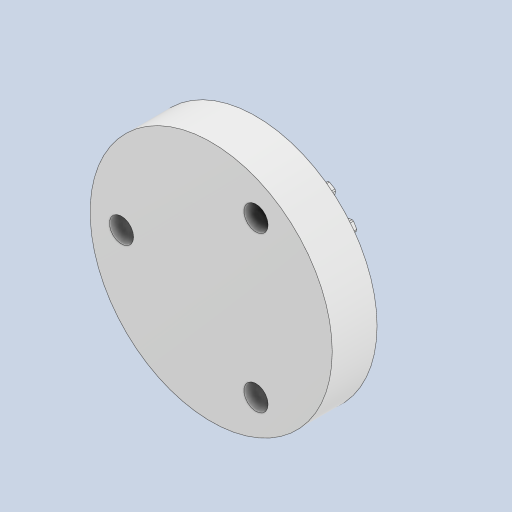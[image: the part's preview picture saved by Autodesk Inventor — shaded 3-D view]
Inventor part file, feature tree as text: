
AUTODESK INVENTOR PART (.ipt)
format: ipt  version: 2023 (Build 270158000, 158)  size: 304,128 bytes
history: native  units: mm (DEFAULTED — no unit token found)
features: extrude x3, plane x3, other x3, sketch x3, chamfer x1, fillet x1
ambient origin geometry x8: Origin, YZ Plane, XZ Plane, XY Plane, X Axis, Y Axis, Z Axis, Center Point
bodies: Solid1 (feature_tree)
feature tree (14):
  extrude  "Extrusion1"  Depth=5.0mm TaperAngle=0.0deg
  plane  "Work Plane2"
  plane  "Work Plane8"
  plane  "Work Plane9"
  other  "平歯車"
  sketch  "スケッチ5"
  extrude  "押し出し3"  Depth=10.0mm TaperAngle=0.0deg
  extrude  "押し出し4"  Depth=0.3mm
  chamfer  "面取り1"  Angle=15.0deg  [1 undecoded]
  fillet  "フィレット1"  [1 undecoded]
  sketch  "Sketch1"  dims[d0=14.0mm d1=5.0mm d2=0.0mm]
  sketch  "Sketch2"  dims[d3=12.0mm d4=10.0mm d5=0.0mm d16=12.0mm d17=0.0mm d34=15.0deg d39=0.0mm d41=0.0mm d43=12.0mm d46=12.0mm d47=0.0mm d48=0.0mm d51=27.0mm d52=5.0mm d53=2.7mm d54=10.0mm d55=30.0mm d57=360.0deg d59=5.0mm d60=0.0mm d61=3.0mm d62=0.0mm d63=0.1mm d64=2.0mm d65=45.0deg d66=0.3mm]
  other  "Srf1"
  other  "ピッチ円直径"
note: 2 required parameter values undecoded (feature->parameter linkage not recoverable at this tier; creation-order binding heuristic only, values carry confidence <= 0.55)
